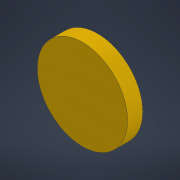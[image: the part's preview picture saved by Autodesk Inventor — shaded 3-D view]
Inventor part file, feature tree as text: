
AUTODESK INVENTOR PART (.ipt)
format: ipt  version: 2021 (Build 250183000, 183)  size: 94,208 bytes
history: native  units: mm
features: extrude x1, sketch x1
ambient origin geometry x8: Origin, YZ Plane, XZ Plane, XY Plane, X Axis, Y Axis, Z Axis, Center Point
bodies: Solid1 (feature_tree)
feature tree (2):
  extrude  "Extrusion1"  Depth=10.0mm
  sketch  "Sketch1"  dims[d0=10.0mm d1=0.0mm d2=60.0mm]
